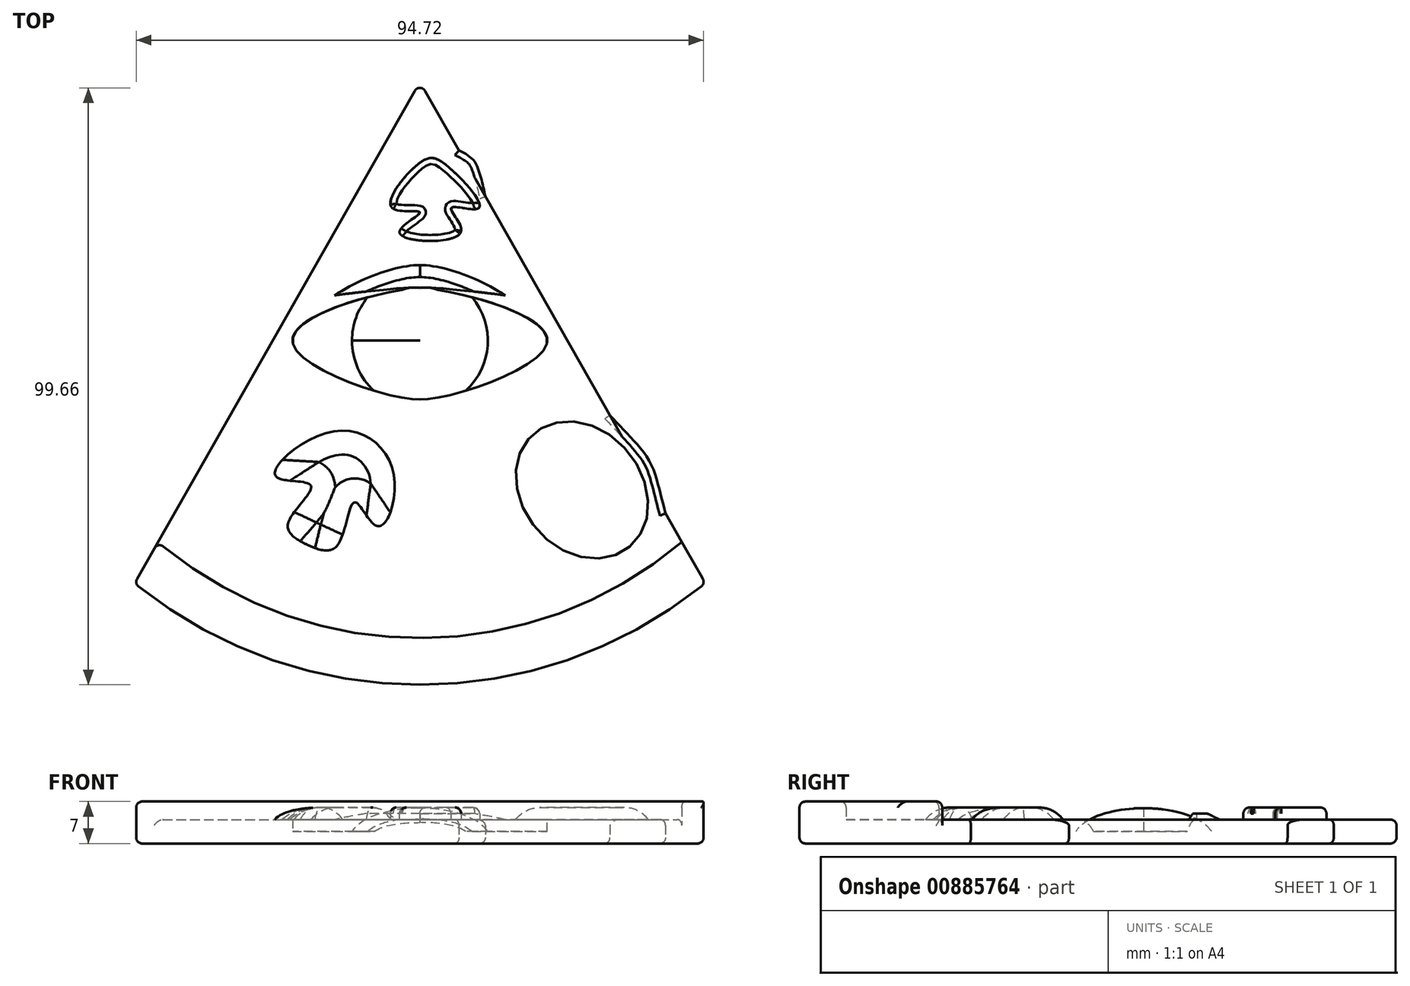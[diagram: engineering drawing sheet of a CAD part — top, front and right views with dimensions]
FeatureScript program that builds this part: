
annotation { "Feature Type Name" : "Feature", "Feature Type Description" : "" }
export const myFeature = defineFeature(function(context is Context, id is Id, definition is map)
    precondition{}
    {
        {
            var Q0;
            Q0=qCreatedBy(makeId("Top.planeOp"),FACE);
            var sketch = newSketch(context, id + "F0", { "sketchPlane" : qUnion([Q0])});
            skArc(sketch, "E0", {"start": v(-47.65, -58.5) * mm, "mid": v(0, -75.46) * mm, "end": v(47.65, -58.5) * mm});
            skLineSegment(sketch, "E1", {"start": v(-47.65, -58.5) * mm, "end": v(0, 25.22) * mm});
            skLineSegment(sketch, "E2", {"start": v(0, 25.22) * mm, "end": v(47.65, -58.5) * mm});
            skFitSpline(sketch, "E3", {"points": [v(6.53, 13.75) * mm, v(9.6, 10.98) * mm, v(10.93, 6.03) * mm], "startDerivative": vector(15.63, -7.53) * mm, "endDerivative": vector(3.12, -16.5) * mm});
            skFitSpline(sketch, "E4", {"points": [v(31.68, -30.45) * mm, v(38.32, -38.11) * mm, v(41, -46.83) * mm], "startDerivative": vector(20.18, -21.32) * mm, "endDerivative": vector(7.37, -27.6) * mm});
            skSolve(sketch);
        }
        {
            var Q0;
            Q0 = qSketchRegion(id + "F0", true);
            extrude(context, id + "F1", {"entities" : qUnion([Q0]), "depth" : 4 * mm, "offsetDistance" : 25 * mm});
        }
        {
            var Q0;
            Q0=makeQuery(id+"F1.opExtrude","CAP_FACE",FACE,{"disambiguationData":[OSD([sQuery(id+"F0.wireOp",EDGE,"E0"),sQuery(id+"F0.wireOp",EDGE,"E1"),sQuery(id+"F0.wireOp",EDGE,"E2")])],"isStart":false});
            var sketch = newSketch(context, id + "F2", { "sketchPlane" : qUnion([Q0])});
            skArc(sketch, "E5.0", {"start": v(-47.65, -58.5) * mm, "mid": v(0, -75.46) * mm, "end": v(47.65, -58.5) * mm});
            skArc(sketch, "E6.0", {"start": v(-43.73, -51.62) * mm, "mid": v(0, -67.66) * mm, "end": v(43.73, -51.62) * mm});
            skLineSegment(sketch, "E7", {"start": v(-43.73, -51.62) * mm, "end": v(-47.65, -58.5) * mm});
            skLineSegment(sketch, "E8", {"start": v(43.73, -51.62) * mm, "end": v(47.65, -58.5) * mm});
            skSolve(sketch);
        }
        {
            var Q0;
            Q0=makeQuery(id+"F2.imprint","IMPRINT",FACE,{"disambiguationData":[TD([[makeQuery(id+"F2.imprint","IMPRINT",EDGE,{"derivedFrom":sQuery(id+"F2.wireOp",EDGE,"E5.0")}),1.0]])]});
            extrude(context, id + "F3", {"entities" : qUnion([Q0]), "operationType" : NewBodyOperationType.ADD, "depth" : 3 * mm, "offsetDistance" : 25 * mm});
        }
        {
            var Q0;
            Q0=makeQuery(id+"F1.opExtrude","CAP_FACE",FACE,{"disambiguationData":[OSD([sQuery(id+"F0.wireOp",EDGE,"E0"),sQuery(id+"F0.wireOp",EDGE,"E1"),sQuery(id+"F0.wireOp",EDGE,"E2")])],"isStart":false});
            var sketch = newSketch(context, id + "F4", { "sketchPlane" : qUnion([Q0])});
            skFitSpline(sketch, "E9", {"points": [v(0, -9.18) * mm, v(21.26, -17.99) * mm, v(0, -27.8) * mm], "startDerivative": vector(32.48, -1.51) * mm, "endDerivative": vector(-27.73, 1.5) * mm});
            skFitSpline(sketch, "E10.MirrorCS", {"points": [v(0, -9.18) * mm, v(-21.26, -17.99) * mm, v(0, -27.8) * mm], "startDerivative": vector(-32.48, -1.51) * mm, "endDerivative": vector(27.73, 1.5) * mm});
            skSolve(sketch);
        }
        {
            var Q0;
            Q0=makeQuery(id+"F4.imprint","IMPRINT",FACE,{"disambiguationData":[TD([[makeQuery(id+"F4.imprint","IMPRINT",EDGE,{"derivedFrom":sQuery(id+"F4.wireOp",EDGE,"E9")}),-1.0]])]});
            extrude(context, id + "F5", {"entities" : qUnion([Q0]), "operationType" : NewBodyOperationType.REMOVE, "oppositeDirection" : true, "depth" : 2 * mm, "offsetDistance" : 25 * mm});
        }
        {
            var Q0;
            Q0=makeQuery(id+"F1.opExtrude","CAP_FACE",FACE,{"disambiguationData":[OSD([sQuery(id+"F0.wireOp",EDGE,"E0"),sQuery(id+"F0.wireOp",EDGE,"E1"),sQuery(id+"F0.wireOp",EDGE,"E2")])],"isStart":false});
            var sketch = newSketch(context, id + "F6", { "sketchPlane" : qUnion([Q0])});
            skFitSpline(sketch, "E11.0", {"points": [v(0, -9.18) * mm, v(-5.39, -9.43) * mm, v(-37.5, -17.31) * mm, v(-4.64, -28.05) * mm, v(0, -27.8) * mm]});
            skFitSpline(sketch, "E12.0", {"points": [v(0, -9.18) * mm, v(5.39, -9.43) * mm, v(37.5, -17.31) * mm, v(4.64, -28.05) * mm, v(0, -27.8) * mm]});
            skFitSpline(sketch, "E13", {"points": [v(-21.23, -17.6) * mm, v(0, -5.38) * mm], "startDerivative": vector(7.53, 18.15) * mm, "endDerivative": vector(20.39, 0) * mm});
            skFitSpline(sketch, "E14.MirrorCS", {"points": [v(21.23, -17.6) * mm, v(0, -5.38) * mm], "startDerivative": vector(-7.53, 18.15) * mm, "endDerivative": vector(-20.39, 0) * mm});
            skPoint(sketch, "E15.orphan", {"position": v(0, -27.8) * mm});
            skSolve(sketch);
        }
        {
            var Q0;
            {var subQ0=sQuery(id+"F6.wireOp",EDGE,"E12.0");var subQ1=sQuery(id+"F6.wireOp",EDGE,"E11.0");var subQ2=makeQuery(id+"F6.imprint","INTERSECT",VERTEX,{"derivedFrom":[subQ1,subQ0]});Q0=makeQuery(id+"F6.imprint","IMPRINT",FACE,{"disambiguationData":[TD([[makeQuery(id+"F6.imprint","IMPRINT",EDGE,{"disambiguationData":[TD([[subQ2,-1.0]])],"derivedFrom":subQ1}),-1.0]])]});}
            extrude(context, id + "F7", {"entities" : qUnion([Q0]), "operationType" : NewBodyOperationType.ADD, "depth" : 1 * mm, "offsetDistance" : 25 * mm});
        }
        {
            var Q0;
            Q0=qCreatedBy(makeId("Front.planeOp"),FACE);
            cPlane(context, id + "F8", {"entities" : qUnion([Q0]), "cplaneType" : CPlaneType.OFFSET, "offset" : 18 * mm, "width" : 150 * mm, "height" : 150 * mm});
        }
        {
            var Q0;
            Q0=qCreatedBy(id+"F8.planeOp",FACE);
            var sketch = newSketch(context, id + "F9", { "sketchPlane" : qUnion([Q0])});
            skFitSpline(sketch, "E16.0", {"points": [v(0, 3) * mm, v(-7.09, 3) * mm, v(-14.18, 3) * mm, v(-21.26, 3) * mm], "construction": true});
            skLineSegment(sketch, "E17", {"start": v(0, 2) * mm, "end": v(0, 5.9) * mm});
            skLineSegment(sketch, "E18", {"start": v(0, 2) * mm, "end": v(-11.34, 2) * mm});
            skFitSpline(sketch, "E19", {"points": [v(0, 5.9) * mm, v(-11.34, 2) * mm], "startDerivative": vector(-11.93, 0) * mm, "endDerivative": vector(-5.98, -8.73) * mm});
            skSolve(sketch);
        }
        {
            var Q0;
            Q0=makeQuery(id+"F9.imprint","IMPRINT",FACE,{"disambiguationData":[TD([[makeQuery(id+"F9.imprint","IMPRINT",EDGE,{"derivedFrom":sQuery(id+"F9.wireOp",EDGE,"E17")}),1.0]])]});
            var Q1;
            Q1=sQuery(id+"F9.wireOp",EDGE,"E17");
            revolve(context, id + "F10", {"operationType" : NewBodyOperationType.ADD, "surfaceOperationType" : NewSurfaceOperationType.NEW, "entities" : qUnion([Q0]), "axis" : qUnion([Q1]), "revolveType" : RevolveType.FULL});
        }
        {
            var Q0;
            Q0=makeQuery(id+"F7.opExtrude","CAP_EDGE",EDGE,{"disambiguationData":[OSD([sQuery(id+"F6.wireOp",EDGE,"E13")])],"isStart":false});
            chamfer(context, id + "F11", {"entities" : qUnion([Q0]), "chamferType" : ChamferType.TWO_OFFSETS, "width1" : 1 * mm, "oppositeDirection" : false, "width2" : 2 * mm, "tangentPropagation" : true});
        }
        {
            var Q0;
            Q0=makeQuery(id+"F1.opExtrude","CAP_FACE",FACE,{"disambiguationData":[OSD([sQuery(id+"F0.wireOp",EDGE,"E0"),sQuery(id+"F0.wireOp",EDGE,"E1"),sQuery(id+"F0.wireOp",EDGE,"E2")])],"isStart":false});
            var sketch = newSketch(context, id + "F12", { "sketchPlane" : qUnion([Q0])});
            skEllipse(sketch, "E20", {"center": v(27.05, -42.93) * mm, "majorRadius": 12.38 * mm, "minorRadius": 10.02 * mm, "majorAxis": v(0.64, -0.77)});
            skFitSpline(sketch, "E21", {"points": [v(-18.66, -52.14) * mm, v(-22, -48.5) * mm, v(-18.23, -42.18) * mm, v(-24.06, -40.63) * mm, v(-14.45, -33.16) * mm, v(-4.37, -40.38) * mm, v(-7.14, -48.95) * mm, v(-10.86, -45) * mm, v(-13.76, -52.15) * mm, v(-18.66, -52.14) * mm]});
            skFitSpline(sketch, "E22", {"points": [v(-3.39, 0) * mm, v(0, 3.4) * mm, v(-4.66, 4.17) * mm, v(0, 11.7) * mm, v(4.21, 11.45) * mm, v(9.8, 4.13) * mm, v(5.23, 4.14) * mm, v(6.76, 0) * mm, v(-3.39, 0) * mm]});
            skSolve(sketch);
        }
        {
            var Q0;
            Q0=makeQuery(id+"F12.imprint","IMPRINT",FACE,{"disambiguationData":[TD([[makeQuery(id+"F12.imprint","IMPRINT",EDGE,{"derivedFrom":sQuery(id+"F12.wireOp",EDGE,"E20")}),1.0]])]});
            var Q1;
            Q1=makeQuery(id+"F12.imprint","IMPRINT",FACE,{"disambiguationData":[TD([[makeQuery(id+"F12.imprint","IMPRINT",EDGE,{"derivedFrom":sQuery(id+"F12.wireOp",EDGE,"E21")}),-1.0]])]});
            var Q2;
            Q2=makeQuery(id+"F12.imprint","IMPRINT",FACE,{"disambiguationData":[TD([[makeQuery(id+"F12.imprint","IMPRINT",EDGE,{"derivedFrom":sQuery(id+"F12.wireOp",EDGE,"E22")}),-1.0]])]});
            extrude(context, id + "F13", {"entities" : qUnion([Q0, Q1, Q2]), "operationType" : NewBodyOperationType.ADD, "depth" : 2 * mm, "offsetDistance" : 25 * mm});
        }
        {
            var Q0;
            Q0=makeQuery(id+"F1.opExtrude","CAP_EDGE",EDGE,{"disambiguationData":[OSD([sQuery(id+"F0.wireOp",EDGE,"E1")])],"isStart":false});
            var Q1;
            Q1=makeQuery(id+"F3.opExtrude","CAP_EDGE",EDGE,{"disambiguationData":[OSD([sQuery(id+"F2.wireOp",EDGE,"E6.0")])],"isStart":false});
            var Q2;
            Q2=makeQuery(id+"F3.opExtrude","CAP_EDGE",EDGE,{"disambiguationData":[OSD([sQuery(id+"F2.wireOp",EDGE,"E5.0")])],"isStart":false});
            var Q3;
            Q3=makeQuery(id+"F1.opExtrude","CAP_EDGE",EDGE,{"disambiguationData":[OSD([sQuery(id+"F0.wireOp",EDGE,"E0")])],"isStart":true});
            var Q4;
            Q4=makeQuery(id+"F3.boolean.opBoolean","MERGE",EDGE,{"derivedFrom":[makeQuery(id+"F1.opExtrude","SWEPT_EDGE",EDGE,{"disambiguationData":[OSD([sQuery(id+"F0.wireOp",EDGE,"E0"),sQuery(id+"F0.wireOp",EDGE,"E2")])]}),makeQuery(id+"F3.opExtrude","SWEPT_EDGE",EDGE,{"disambiguationData":[OSD([sQuery(id+"F2.wireOp",EDGE,"E5.0"),sQuery(id+"F2.wireOp",EDGE,"E8")])]})]});
            var Q5;
            Q5=makeQuery(id+"F3.boolean.opBoolean","MERGE",EDGE,{"derivedFrom":[makeQuery(id+"F1.opExtrude","SWEPT_EDGE",EDGE,{"disambiguationData":[OSD([sQuery(id+"F0.wireOp",EDGE,"E0"),sQuery(id+"F0.wireOp",EDGE,"E1")])]}),makeQuery(id+"F3.opExtrude","SWEPT_EDGE",EDGE,{"disambiguationData":[OSD([sQuery(id+"F2.wireOp",EDGE,"E5.0"),sQuery(id+"F2.wireOp",EDGE,"E7")])]})]});
            var Q6;
            Q6=makeQuery(id+"F3.boolean.opBoolean","MERGE",FACE,{"derivedFrom":[makeQuery(id+"F1.opExtrude","SWEPT_FACE",FACE,{"disambiguationData":[OSD([sQuery(id+"F0.wireOp",EDGE,"E1")])]}),makeQuery(id+"F3.opExtrude","SWEPT_FACE",FACE,{"disambiguationData":[OSD([sQuery(id+"F2.wireOp",EDGE,"E7")])]})]});
            var Q7;
            Q7=makeQuery(id+"F1.opExtrude","CAP_EDGE",EDGE,{"disambiguationData":[OSD([sQuery(id+"F0.wireOp",EDGE,"E2")])],"isStart":true});
            var Q8;
            Q8=makeQuery(id+"F1.opExtrude","CAP_EDGE",EDGE,{"disambiguationData":[OSD([sQuery(id+"F0.wireOp",EDGE,"E1")])],"isStart":true});
            var Q9;
            Q9=makeQuery(id+"F1.opExtrude","CAP_EDGE",EDGE,{"disambiguationData":[OSD([sQuery(id+"F0.wireOp",EDGE,"E3")])],"isStart":false});
            var Q10;
            Q10=makeQuery(id+"F1.opExtrude","CAP_EDGE",EDGE,{"disambiguationData":[OSD([sQuery(id+"F0.wireOp",EDGE,"E3")])],"isStart":true});
            var Q11;
            Q11=makeQuery(id+"F1.opExtrude","CAP_EDGE",EDGE,{"disambiguationData":[OSD([sQuery(id+"F0.wireOp",EDGE,"E4")])],"isStart":false});
            var Q12;
            {var subQ0=sQuery(id+"F0.wireOp",EDGE,"E2");Q12=makeQuery(id+"F1.opExtrude","CAP_EDGE",EDGE,{"disambiguationData":[OSD([subQ0]),TDD([makeQuery(id+"F0.imprint","IMPRINT",EDGE,{"disambiguationData":[TD([[makeQuery(id+"F0.imprint","INTERSECT",VERTEX,{"derivedFrom":[sQuery(id+"F0.wireOp",EDGE,"E1"),subQ0]}),-1.0]])],"derivedFrom":subQ0})])],"isStart":false});}
            var Q13;
            {var subQ0=sQuery(id+"F0.wireOp",EDGE,"E2");Q13=makeQuery(id+"F1.opExtrude","CAP_EDGE",EDGE,{"disambiguationData":[OSD([subQ0]),TDD([makeQuery(id+"F0.imprint","IMPRINT",EDGE,{"disambiguationData":[TD([[makeQuery(id+"F0.imprint","INTERSECT",VERTEX,{"disambiguationData":[OD(1.0)],"derivedFrom":[subQ0,sQuery(id+"F0.wireOp",EDGE,"E3")]}),-1.0]])],"derivedFrom":subQ0})])],"isStart":false});}
            var Q14;
            {var subQ0=sQuery(id+"F0.wireOp",EDGE,"E2");Q14=makeQuery(id+"F1.opExtrude","CAP_EDGE",EDGE,{"disambiguationData":[OSD([subQ0]),TDD([makeQuery(id+"F0.imprint","IMPRINT",EDGE,{"disambiguationData":[TD([[makeQuery(id+"F0.imprint","INTERSECT",VERTEX,{"derivedFrom":[sQuery(id+"F0.wireOp",EDGE,"E0"),subQ0]}),1.0]])],"derivedFrom":subQ0})])],"isStart":false});}
            var Q15;
            Q15=makeQuery(id+"F1.opExtrude","CAP_EDGE",EDGE,{"disambiguationData":[OSD([sQuery(id+"F0.wireOp",EDGE,"E4")])],"isStart":true});
            fillet(context, id + "F14", {"entities" : qUnion([Q0, Q1, Q2, Q3, Q4, Q5, Q6, Q7, Q8, Q9, Q10, Q11, Q12, Q13, Q14, Q15]), "radius" : 1 * mm, "tangentPropagation" : true, "allowEdgeOverflow" : false});
        }
        {
            var Q0;
            Q0=makeQuery(id+"F13.opExtrude","CAP_FACE",FACE,{"disambiguationData":[OSD([sQuery(id+"F12.wireOp",EDGE,"E20")])],"isStart":false});
            var Q1;
            Q1=makeQuery(id+"F13.opExtrude","CAP_FACE",FACE,{"disambiguationData":[OSD([sQuery(id+"F12.wireOp",EDGE,"E21")])],"isStart":false});
            fillet(context, id + "F15", {"entities" : qUnion([Q0, Q1]), "radius" : 5 * mm, "tangentPropagation" : true, "allowEdgeOverflow" : false});
        }
        {
            var Q0;
            Q0=makeQuery(id+"F13.opExtrude","CAP_FACE",FACE,{"disambiguationData":[OSD([sQuery(id+"F12.wireOp",EDGE,"E22")])],"isStart":false});
            fillet(context, id + "F16", {"entities" : qUnion([Q0]), "radius" : 1 * mm, "tangentPropagation" : true, "allowEdgeOverflow" : false});
        }
    });
